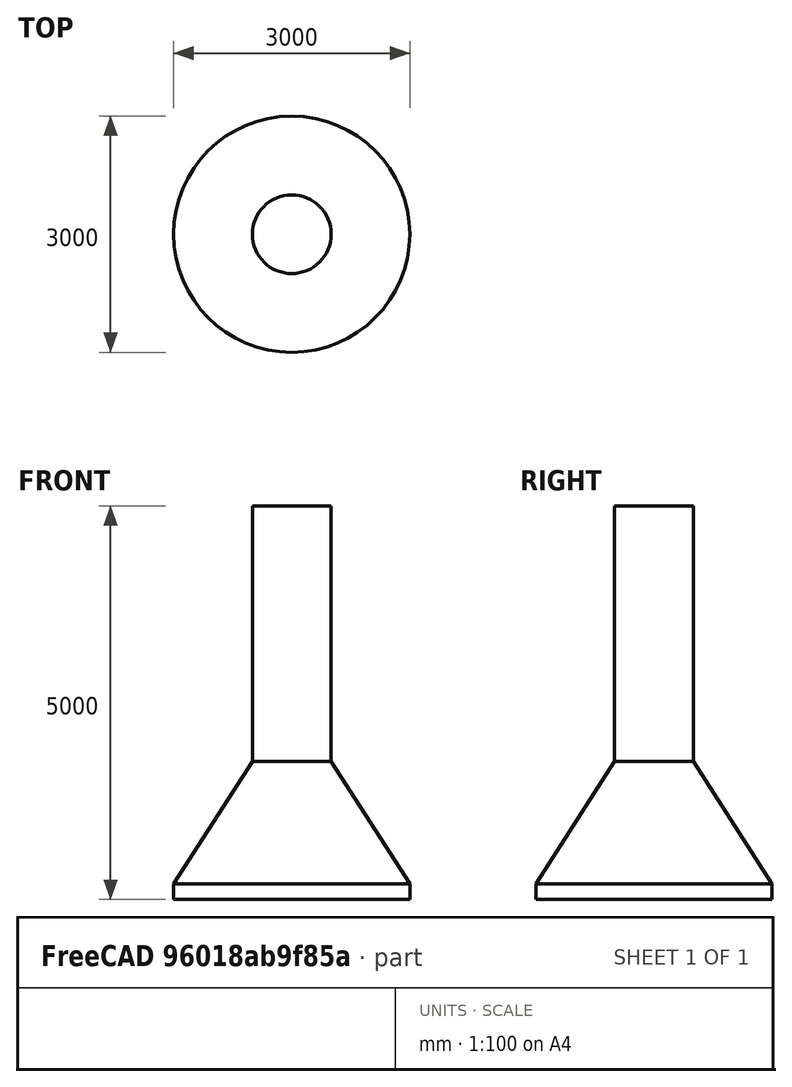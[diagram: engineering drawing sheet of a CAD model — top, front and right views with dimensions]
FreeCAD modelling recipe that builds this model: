
FCSTD DOCUMENT  (FreeCAD 0.16R6704 (Git))
Label: Caisson
License: All rights reserved
LicenseURL: http://en.wikipedia.org/wiki/All_rights_reserved
objects: Sketcher::SketchObject×1, PartDesign::Revolution×1
note: 3 computed .brp shape members not serialized (recipe doc carries the construction recipe); baked Part::Feature solids carry a one-line shape summary decoded from their .brp

FEATURE [Sketcher::SketchObject] Sketch071  label="Caisson_dimensions"
  Placement = pos=(0,0,0) rot=(1,0,0;1.5708rad)
  sketch-geometry (7):
    g0: LineSegment [constr] StartX=0 StartY=1849.72 StartZ=0 EndX=0 EndY=-8640.75 EndZ=0
    g1: LineSegment StartX=0 StartY=0 StartZ=0 EndX=500 EndY=0 EndZ=0
    g2: LineSegment StartX=500 StartY=0 StartZ=0 EndX=500 EndY=-3250 EndZ=0
    g3: LineSegment StartX=500 StartY=-3250 StartZ=0 EndX=1500 EndY=-4800 EndZ=0
    g4: LineSegment StartX=1500 StartY=-4800 StartZ=0 EndX=1500 EndY=-5000 EndZ=0
    g5: LineSegment StartX=1500 StartY=-5000 StartZ=0 EndX=0 EndY=-5000 EndZ=0
    g6: LineSegment StartX=0 StartY=-5000 StartZ=0 EndX=0 EndY=0 EndZ=0
  constraints (19):
    c: Vertical(g0)
    c: PointOnObject(g-1,g0)
    c: Coincident(g-1,g1)
    c: Horizontal(g1)
    c: Coincident(g1,g2)
    c: Vertical(g2)
    c: Coincident(g2,g3)
    c: Coincident(g3,g4)
    c: Coincident(g4,g5)
    c: PointOnObject(g5,g0)
    c: Horizontal(g5)
    c: Coincident(g5,g6)
    c: Coincident(g6,g1)
    c: Vertical(g4)
    c: DistanceX(g5,g4) = 1500  'B/2'
    c: DistanceY(g4,g3) = 200  'h'
    c: DistanceX(g-1,g1) = 500  'F/2'
    c: DistanceY(g2,g1) = 3250  'Hf'
    c: DistanceY(g4,g2) = 1750  'Hb'
FEATURE [PartDesign::Revolution] Revolution  label="Caisson "
  Angle = 360
  Axis = (0,0,1)
  Base = (0,0,0)
  Placement = pos=(0,0,0) rot=(1,0,0;1.5708rad)
  ReferenceAxis = -> Sketch071 [V_Axis]
  Reversed = true
  Sketch = -> Sketch071
